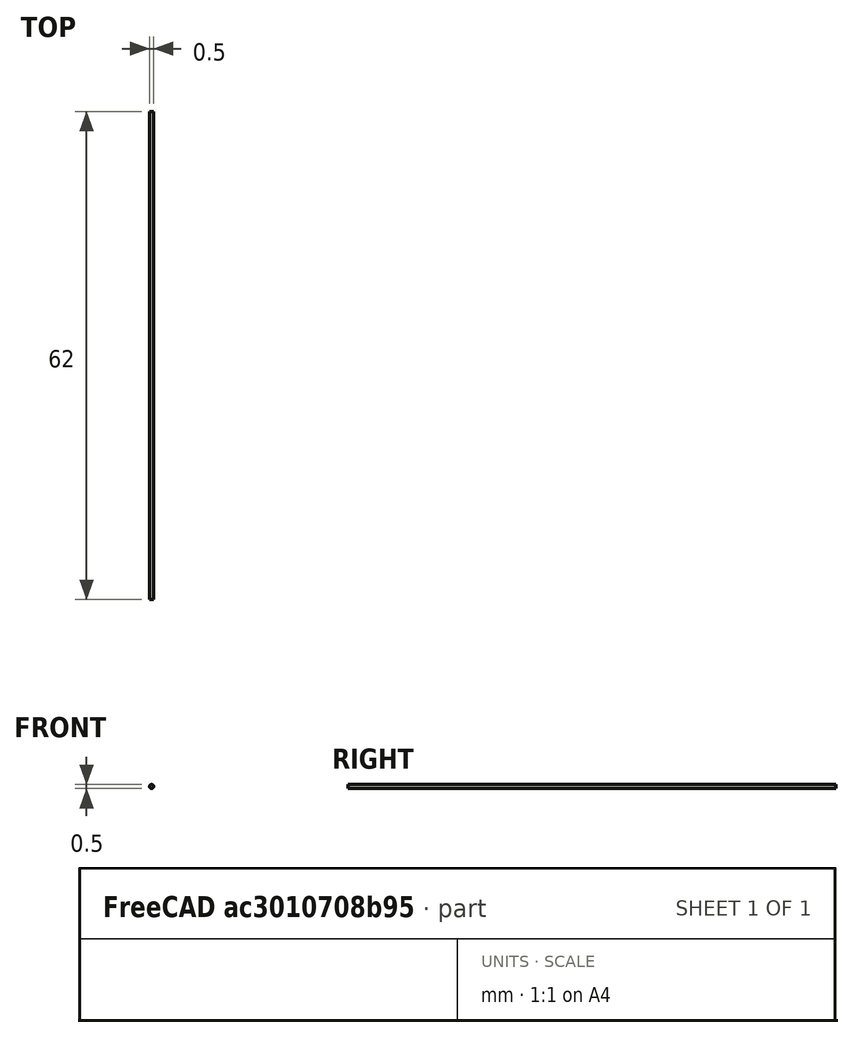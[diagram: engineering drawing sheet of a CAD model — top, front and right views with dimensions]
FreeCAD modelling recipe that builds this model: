
FCSTD DOCUMENT  (FreeCAD 1.1R41365 (Git))
Label: FlexureWire
License: All rights reserved
LicenseURL: https://en.wikipedia.org/wiki/All_rights_reserved
objects: App::Point×1, Sketcher::SketchObject×1, PartDesign::Pad×1, PartDesign::Body×1
note: 6 computed .brp shape members not serialized (recipe doc carries the construction recipe); baked Part::Feature solids carry a one-line shape summary decoded from their .brp

FEATURE [App::Point] Origin001
  Role = Origin
FEATURE [Sketcher::SketchObject] Sketch
  ArcFitTolerance = 1e-06
  AttachmentSupport = -> [XZ_Plane]
  ExternalTypes = [0]
  FullyConstrained = true
  MakeInternals = false
  MapMode = 5
  Placement = pos=(0,0,0) rot=(1,0,0;1.5708rad)
  sketch-geometry (1):
    g0: Circle CenterX=0 CenterY=0 CenterZ=0 NormalX=0 NormalY=0 NormalZ=1 AngleXU=0 Radius=0.25
  constraints (2):
    c: Coincident(g0,g-1)
    c: Diameter(g0) = 0.5
FEATURE [PartDesign::Pad] Pad
  Direction = (0,-1,0)
  Length = 62
  Length2 = 10
  Placement = pos=(0,0,0) rot=(1,0,0;1.5708rad)
  Profile = -> Sketch
  ReferenceAxis = -> Sketch [N_Axis]
  Refine = true
  Suppressed = false
  Type = 0
FEATURE [PartDesign::Body] Body  label="FlexureWire"
  AllowCompound = false
  Group = -> [Sketch,Pad]
  Origin = -> Origin
  Tip = -> Pad
